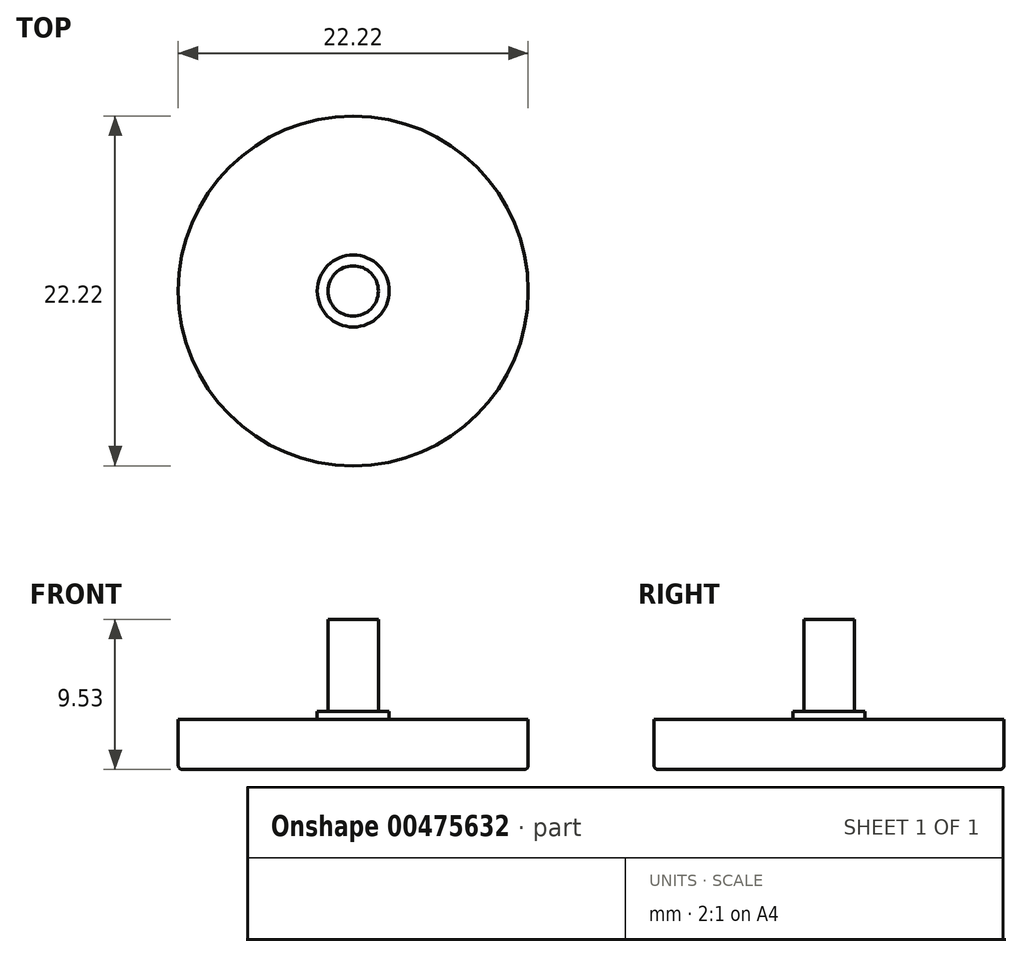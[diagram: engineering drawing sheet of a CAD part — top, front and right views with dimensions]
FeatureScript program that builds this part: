
annotation { "Feature Type Name" : "Feature", "Feature Type Description" : "" }
export const myFeature = defineFeature(function(context is Context, id is Id, definition is map)
    precondition{}
    {
        {
            var Q0;
            Q0=qCreatedBy(makeId("Top.planeOp"),FACE);
            var sketch = newSketch(context, id + "F0", { "sketchPlane" : qUnion([Q0])});
            skCircle(sketch, "E0", {"center": v(0, 0) * mm, "radius": 11.11 * mm});
            skCircle(sketch, "E1", {"center": v(0, 0) * mm, "radius": 1.6 * mm});
            skSolve(sketch);
        }
        {
            var Q0;
            Q0=makeQuery(id+"F0.imprint","IMPRINT",FACE,{"disambiguationData":[TD([[makeQuery(id+"F0.imprint","IMPRINT",EDGE,{"derivedFrom":sQuery(id+"F0.wireOp",EDGE,"E1")}),1.0]])]});
            extrude(context, id + "F1", {"entities" : qUnion([Q0]), "depth" : 9.52 * mm});
        }
        {
            var Q0;
            Q0=qSketchRegion(id+"F0",true);
            extrude(context, id + "F2", {"entities" : qUnion([Q0]), "operationType" : NewBodyOperationType.ADD, "depth" : 3.17 * mm});
        }
        {
            var Q0;
            Q0=makeQuery(id+"F2.opExtrude","CAP_EDGE",EDGE,{"disambiguationData":[OSD([sQuery(id+"F0.wireOp",EDGE,"E0")])],"isStart":true});
            fillet(context, id + "F3", {"entities" : qUnion([Q0]), "radius" : 0.25 * mm, "tangentPropagation" : true, "allowEdgeOverflow" : false});
        }
        {
            var Q0;
            Q0=makeQuery(id+"F1.opExtrude","CAP_FACE",FACE,{"disambiguationData":[OSD([sQuery(id+"F0.wireOp",EDGE,"E1")])],"isStart":false});
            var sketch = newSketch(context, id + "F4", { "sketchPlane" : qUnion([Q0])});
            skCircle(sketch, "E2", {"center": v(0, 0) * mm, "radius": 2.29 * mm});
            skSolve(sketch);
        }
        {
            var Q0;
            Q0=makeQuery(id+"F4.imprint","IMPRINT",FACE,{"disambiguationData":[TD([[makeQuery(id+"F4.imprint","IMPRINT",EDGE,{"derivedFrom":sQuery(id+"F4.wireOp",EDGE,"E2")}),1.0]])]});
            extrude(context, id + "F5", {"entities" : qUnion([Q0]), "operationType" : NewBodyOperationType.ADD, "oppositeDirection" : true, "depth" : 6.35 * mm});
        }
        {
            var Q0;
            {var subQ0=sQuery(id+"F0.wireOp",EDGE,"E1");Q0=makeQuery(id+"F5.boolean.opBoolean","MERGE",FACE,{"derivedFrom":[makeQuery(id+"F1.opExtrude","CAP_FACE",FACE,{"disambiguationData":[OSD([subQ0])],"isStart":false}),makeQuery(id+"F5.opExtrude","CAP_FACE",FACE,{"disambiguationData":[OSD([subQ0,sQuery(id+"F4.wireOp",EDGE,"E2")])],"isStart":true})]});}
            var sketch = newSketch(context, id + "F6", { "sketchPlane" : qUnion([Q0])});
            skCircle(sketch, "E3", {"center": v(0, 0) * mm, "radius": 1.6 * mm});
            skSolve(sketch);
        }
        {
            var Q0;
            Q0=makeQuery(id+"F6.imprint","IMPRINT",FACE,{"disambiguationData":[TD([[makeQuery(id+"F6.imprint","IMPRINT",EDGE,{"derivedFrom":sQuery(id+"F6.wireOp",EDGE,"E3")}),-1.0]])]});
            extrude(context, id + "F7", {"entities" : qUnion([Q0]), "operationType" : NewBodyOperationType.REMOVE, "oppositeDirection" : true, "depth" : 5.84 * mm});
        }
    });
